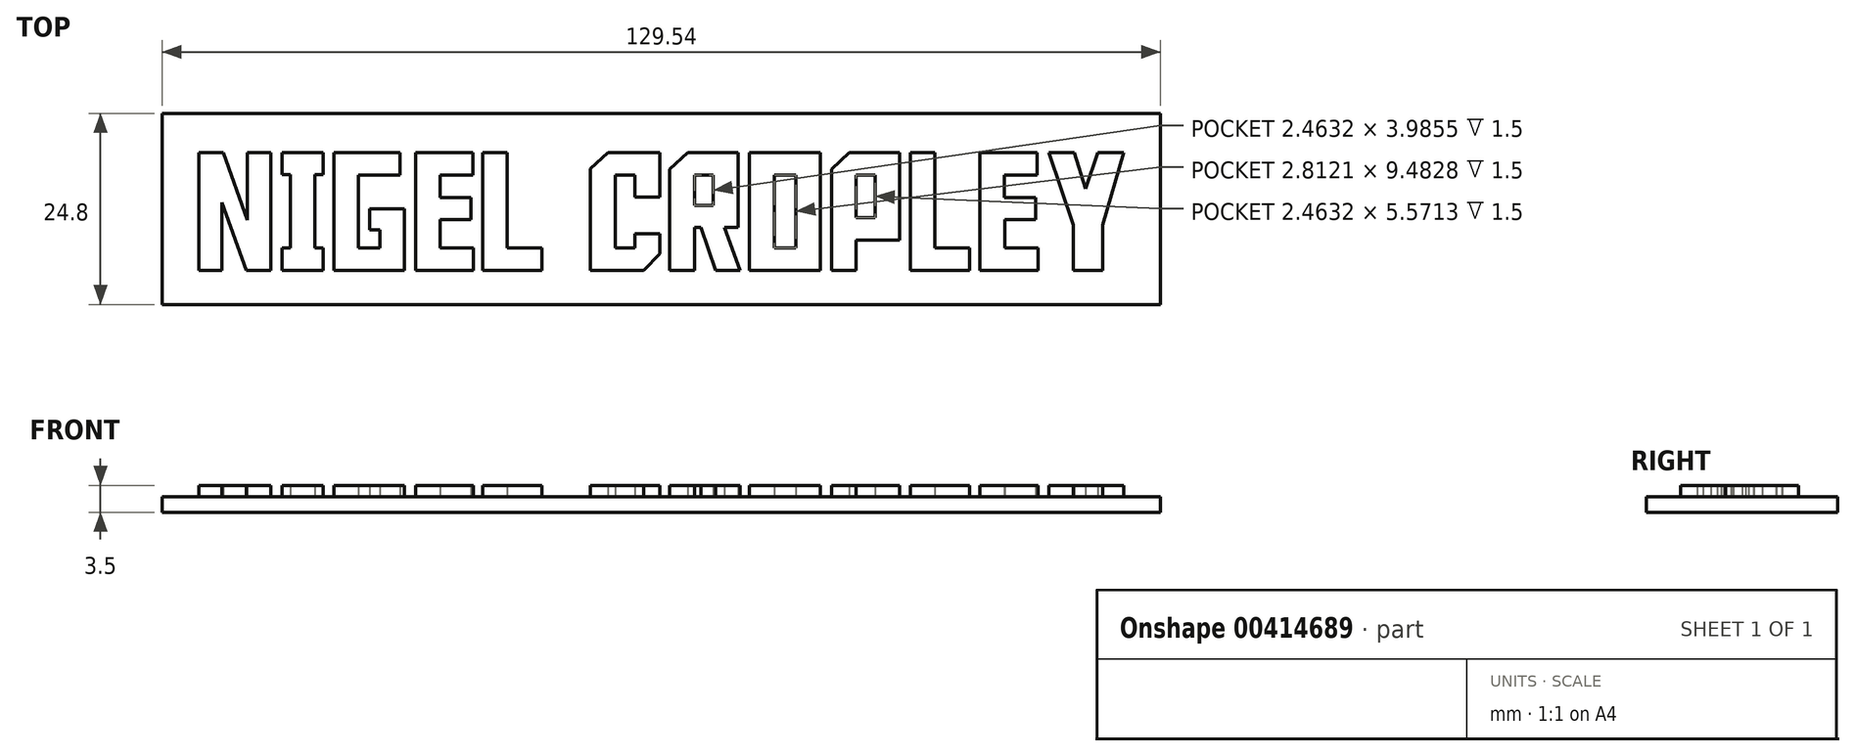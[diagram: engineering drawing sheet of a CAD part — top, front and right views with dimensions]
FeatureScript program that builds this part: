
annotation { "Feature Type Name" : "Feature", "Feature Type Description" : "" }
export const myFeature = defineFeature(function(context is Context, id is Id, definition is map)
    precondition{}
    {
        {
            var Q0;
            Q0=qCreatedBy(makeId("Top.planeOp"),FACE);
            var sketch = newSketch(context, id + "F0", { "sketchPlane" : qUnion([Q0])});
            skLineSegment(sketch, "E0.bottom", {"start": v(-64.77, -12.4) * mm, "end": v(64.77, -12.4) * mm});
            skLineSegment(sketch, "E0.top", {"start": v(-64.77, 12.4) * mm, "end": v(64.77, 12.4) * mm});
            skLineSegment(sketch, "E0.left", {"start": v(-64.77, -12.4) * mm, "end": v(-64.77, 12.4) * mm});
            skLineSegment(sketch, "E0.right", {"start": v(64.77, -12.4) * mm, "end": v(64.77, 12.4) * mm});
            skPoint(sketch, "E0.middle", {"position": v(0, 0) * mm});
            skSolve(sketch);
        }
        {
            var Q0;
            Q0=qCreatedBy(makeId("Top.planeOp"),FACE);
            var sketch = newSketch(context, id + "F1", { "sketchPlane" : qUnion([Q0])});
            skLineSegment(sketch, "E1", {"start": v(-53.72, -1.44) * mm, "end": v(-53.72, 7.33) * mm});
            skLineSegment(sketch, "E2", {"start": v(-53.72, 7.33) * mm, "end": v(-50.7, 7.33) * mm});
            skLineSegment(sketch, "E3", {"start": v(-50.7, 7.33) * mm, "end": v(-50.7, -7.95) * mm});
            skLineSegment(sketch, "E4", {"start": v(-50.7, -7.95) * mm, "end": v(-53.87, -7.95) * mm});
            skLineSegment(sketch, "E5", {"start": v(-53.87, -7.95) * mm, "end": v(-57, 0.82) * mm});
            skLineSegment(sketch, "E6", {"start": v(-57, 0.82) * mm, "end": v(-57, -7.95) * mm});
            skLineSegment(sketch, "E7", {"start": v(-60, -7.95) * mm, "end": v(-60, 7.33) * mm});
            skLineSegment(sketch, "E8", {"start": v(-60, 7.33) * mm, "end": v(-56.83, 7.33) * mm});
            skLineSegment(sketch, "E9", {"start": v(-56.83, 7.33) * mm, "end": v(-53.72, -1.44) * mm});
            skLineSegment(sketch, "E10", {"start": v(-43.88, -5.06) * mm, "end": v(-43.88, -7.95) * mm});
            skLineSegment(sketch, "E11", {"start": v(-43.88, -7.95) * mm, "end": v(-49.2, -7.95) * mm});
            skLineSegment(sketch, "E12", {"start": v(-49.2, -7.95) * mm, "end": v(-49.2, -5.06) * mm});
            skLineSegment(sketch, "E13", {"start": v(-49.2, -5.06) * mm, "end": v(-48.14, -5.06) * mm});
            skLineSegment(sketch, "E14", {"start": v(-48.14, -5.06) * mm, "end": v(-48.14, 4.44) * mm});
            skLineSegment(sketch, "E15", {"start": v(-48.14, 4.44) * mm, "end": v(-49.2, 4.44) * mm});
            skLineSegment(sketch, "E16", {"start": v(-49.2, 4.44) * mm, "end": v(-49.2, 7.33) * mm});
            skLineSegment(sketch, "E17", {"start": v(-49.2, 7.33) * mm, "end": v(-43.88, 7.33) * mm});
            skLineSegment(sketch, "E18", {"start": v(-43.88, 7.33) * mm, "end": v(-43.88, 4.44) * mm});
            skLineSegment(sketch, "E19", {"start": v(-43.88, 4.44) * mm, "end": v(-44.94, 4.44) * mm});
            skLineSegment(sketch, "E20", {"start": v(-44.94, 4.44) * mm, "end": v(-44.94, -5.06) * mm});
            skLineSegment(sketch, "E21", {"start": v(-44.94, -5.06) * mm, "end": v(-43.88, -5.06) * mm});
            skLineSegment(sketch, "E22", {"start": v(-36.54, -5.06) * mm, "end": v(-36.54, -2.7) * mm});
            skLineSegment(sketch, "E23", {"start": v(-36.54, -2.7) * mm, "end": v(-37.84, -2.7) * mm});
            skLineSegment(sketch, "E24", {"start": v(-37.84, -2.7) * mm, "end": v(-37.84, 0.02) * mm});
            skLineSegment(sketch, "E25", {"start": v(-37.84, 0.02) * mm, "end": v(-33.37, 0.02) * mm});
            skLineSegment(sketch, "E26", {"start": v(-33.37, 0.02) * mm, "end": v(-33.37, -7.95) * mm});
            skLineSegment(sketch, "E27", {"start": v(-33.37, -7.95) * mm, "end": v(-42.5, -7.95) * mm});
            skLineSegment(sketch, "E28", {"start": v(-42.5, -7.95) * mm, "end": v(-42.5, 7.33) * mm});
            skLineSegment(sketch, "E29", {"start": v(-42.5, 7.33) * mm, "end": v(-33.9, 7.33) * mm});
            skLineSegment(sketch, "E30", {"start": v(-33.9, 7.33) * mm, "end": v(-33.9, 4.43) * mm});
            skLineSegment(sketch, "E31", {"start": v(-33.9, 4.43) * mm, "end": v(-39.29, 4.43) * mm});
            skLineSegment(sketch, "E32", {"start": v(-39.29, 4.43) * mm, "end": v(-39.29, -5.06) * mm});
            skLineSegment(sketch, "E33", {"start": v(-39.29, -5.06) * mm, "end": v(-36.54, -5.06) * mm});
            skLineSegment(sketch, "E34", {"start": v(-31.9, 7.33) * mm, "end": v(-24.48, 7.33) * mm});
            skLineSegment(sketch, "E35", {"start": v(-24.48, 7.33) * mm, "end": v(-24.48, 4.43) * mm});
            skLineSegment(sketch, "E36", {"start": v(-24.48, 4.43) * mm, "end": v(-28.73, 4.43) * mm});
            skLineSegment(sketch, "E37", {"start": v(-28.73, 4.43) * mm, "end": v(-28.73, 1.48) * mm});
            skLineSegment(sketch, "E38", {"start": v(-28.73, 1.48) * mm, "end": v(-24.7, 1.48) * mm});
            skLineSegment(sketch, "E39", {"start": v(-24.7, 1.48) * mm, "end": v(-24.7, -1.38) * mm});
            skLineSegment(sketch, "E40", {"start": v(-24.7, -1.38) * mm, "end": v(-28.69, -1.38) * mm});
            skLineSegment(sketch, "E41", {"start": v(-28.69, -1.38) * mm, "end": v(-28.69, -5.06) * mm});
            skLineSegment(sketch, "E42", {"start": v(-28.69, -5.06) * mm, "end": v(-24.37, -5.06) * mm});
            skLineSegment(sketch, "E43", {"start": v(-24.37, -5.06) * mm, "end": v(-24.37, -7.95) * mm});
            skLineSegment(sketch, "E44", {"start": v(-24.37, -7.95) * mm, "end": v(-31.9, -7.95) * mm});
            skLineSegment(sketch, "E45", {"start": v(-31.9, -7.95) * mm, "end": v(-31.9, 7.33) * mm});
            skLineSegment(sketch, "E46", {"start": v(-23.2, -7.95) * mm, "end": v(-23.2, 7.33) * mm});
            skLineSegment(sketch, "E47", {"start": v(-23.2, 7.33) * mm, "end": v(-20, 7.33) * mm});
            skLineSegment(sketch, "E48", {"start": v(-20, 7.33) * mm, "end": v(-20, -5.06) * mm});
            skLineSegment(sketch, "E49", {"start": v(-20, -5.06) * mm, "end": v(-15.51, -5.06) * mm});
            skLineSegment(sketch, "E50", {"start": v(-15.51, -5.06) * mm, "end": v(-15.51, -7.95) * mm});
            skLineSegment(sketch, "E51", {"start": v(-15.51, -7.95) * mm, "end": v(-23.2, -7.95) * mm});
            skLineSegment(sketch, "E52", {"start": v(-3.4, -5.06) * mm, "end": v(-3.4, -3.2) * mm});
            skLineSegment(sketch, "E53", {"start": v(-3.4, -3.2) * mm, "end": v(-0.2, -3.2) * mm});
            skLineSegment(sketch, "E54", {"start": v(-0.2, -3.2) * mm, "end": v(-0.2, -5.84) * mm});
            skLineSegment(sketch, "E55", {"start": v(-0.2, -5.84) * mm, "end": v(-2.3, -7.95) * mm});
            skLineSegment(sketch, "E56", {"start": v(-2.3, -7.95) * mm, "end": v(-9.2, -7.95) * mm});
            skLineSegment(sketch, "E57", {"start": v(-9.2, -7.95) * mm, "end": v(-9.2, 5.23) * mm});
            skLineSegment(sketch, "E58", {"start": v(-9.2, 5.23) * mm, "end": v(-6.92, 7.33) * mm});
            skLineSegment(sketch, "E59", {"start": v(-6.92, 7.33) * mm, "end": v(-0.2, 7.33) * mm});
            skLineSegment(sketch, "E60", {"start": v(-0.2, 7.33) * mm, "end": v(-0.2, 1.56) * mm});
            skLineSegment(sketch, "E61", {"start": v(-0.2, 1.56) * mm, "end": v(-3.4, 1.56) * mm});
            skLineSegment(sketch, "E62", {"start": v(-3.4, 1.56) * mm, "end": v(-3.4, 4.43) * mm});
            skLineSegment(sketch, "E63", {"start": v(-3.4, 4.43) * mm, "end": v(-5.99, 4.43) * mm});
            skLineSegment(sketch, "E64", {"start": v(-5.99, 4.43) * mm, "end": v(-5.99, -5.06) * mm});
            skLineSegment(sketch, "E65", {"start": v(-5.99, -5.06) * mm, "end": v(-3.4, -5.06) * mm});
            skLineSegment(sketch, "E66", {"start": v(7.04, -7.95) * mm, "end": v(5.13, -2.42) * mm});
            skLineSegment(sketch, "E67", {"start": v(5.13, -2.42) * mm, "end": v(4.29, -2.42) * mm});
            skLineSegment(sketch, "E68", {"start": v(4.29, -2.42) * mm, "end": v(4.29, -7.95) * mm});
            skLineSegment(sketch, "E69", {"start": v(4.29, -7.95) * mm, "end": v(1.08, -7.95) * mm});
            skLineSegment(sketch, "E70", {"start": v(1.08, -7.95) * mm, "end": v(1.08, 5.18) * mm});
            skLineSegment(sketch, "E71", {"start": v(1.08, 5.18) * mm, "end": v(3.4, 7.33) * mm});
            skLineSegment(sketch, "E72", {"start": v(3.4, 7.33) * mm, "end": v(9.95, 7.33) * mm});
            skLineSegment(sketch, "E73", {"start": v(9.95, 7.33) * mm, "end": v(9.95, -2.38) * mm});
            skLineSegment(sketch, "E74", {"start": v(9.95, -2.38) * mm, "end": v(8.22, -2.38) * mm});
            skLineSegment(sketch, "E75", {"start": v(8.22, -2.38) * mm, "end": v(10.25, -7.95) * mm});
            skLineSegment(sketch, "E76", {"start": v(10.25, -7.95) * mm, "end": v(7.04, -7.95) * mm});
            skLineSegment(sketch, "E77", {"start": v(6.75, 0.44) * mm, "end": v(6.75, 4.43) * mm});
            skLineSegment(sketch, "E78", {"start": v(6.75, 4.43) * mm, "end": v(4.29, 4.43) * mm});
            skLineSegment(sketch, "E79", {"start": v(4.29, 4.43) * mm, "end": v(4.29, 0.44) * mm});
            skLineSegment(sketch, "E80", {"start": v(4.29, 0.44) * mm, "end": v(6.75, 0.44) * mm});
            skLineSegment(sketch, "E81", {"start": v(11.43, 7.33) * mm, "end": v(20.66, 7.33) * mm});
            skLineSegment(sketch, "E82", {"start": v(20.66, 7.33) * mm, "end": v(20.66, -7.95) * mm});
            skLineSegment(sketch, "E83", {"start": v(20.66, -7.95) * mm, "end": v(11.43, -7.95) * mm});
            skLineSegment(sketch, "E84", {"start": v(11.43, -7.95) * mm, "end": v(11.43, 7.33) * mm});
            skLineSegment(sketch, "E85", {"start": v(14.65, -5.06) * mm, "end": v(17.46, -5.06) * mm});
            skLineSegment(sketch, "E86", {"start": v(17.46, -5.06) * mm, "end": v(17.46, 4.43) * mm});
            skLineSegment(sketch, "E87", {"start": v(17.46, 4.43) * mm, "end": v(14.65, 4.43) * mm});
            skLineSegment(sketch, "E88", {"start": v(14.65, 4.43) * mm, "end": v(14.65, -5.06) * mm});
            skLineSegment(sketch, "E89", {"start": v(25.27, -7.95) * mm, "end": v(22.07, -7.95) * mm});
            skLineSegment(sketch, "E90", {"start": v(22.07, -7.95) * mm, "end": v(22.07, 5.18) * mm});
            skLineSegment(sketch, "E91", {"start": v(22.07, 5.18) * mm, "end": v(24.38, 7.33) * mm});
            skLineSegment(sketch, "E92", {"start": v(24.38, 7.33) * mm, "end": v(30.94, 7.33) * mm});
            skLineSegment(sketch, "E93", {"start": v(30.94, 7.33) * mm, "end": v(30.94, -4.07) * mm});
            skLineSegment(sketch, "E94", {"start": v(30.94, -4.07) * mm, "end": v(25.27, -4.07) * mm});
            skLineSegment(sketch, "E95", {"start": v(25.27, -4.07) * mm, "end": v(25.27, -7.95) * mm});
            skLineSegment(sketch, "E96", {"start": v(27.74, -1.14) * mm, "end": v(27.74, 4.43) * mm});
            skLineSegment(sketch, "E97", {"start": v(27.74, 4.43) * mm, "end": v(25.27, 4.43) * mm});
            skLineSegment(sketch, "E98", {"start": v(25.27, 4.43) * mm, "end": v(25.27, -1.14) * mm});
            skLineSegment(sketch, "E99", {"start": v(25.27, -1.14) * mm, "end": v(27.74, -1.14) * mm});
            skLineSegment(sketch, "E100", {"start": v(32.3, -7.95) * mm, "end": v(32.3, 7.33) * mm});
            skLineSegment(sketch, "E101", {"start": v(32.3, 7.33) * mm, "end": v(35.5, 7.33) * mm});
            skLineSegment(sketch, "E102", {"start": v(35.5, 7.33) * mm, "end": v(35.5, -5.06) * mm});
            skLineSegment(sketch, "E103", {"start": v(35.5, -5.06) * mm, "end": v(39.99, -5.06) * mm});
            skLineSegment(sketch, "E104", {"start": v(39.99, -5.06) * mm, "end": v(39.99, -7.95) * mm});
            skLineSegment(sketch, "E105", {"start": v(39.99, -7.95) * mm, "end": v(32.3, -7.95) * mm});
            skLineSegment(sketch, "E106", {"start": v(41.36, 7.33) * mm, "end": v(48.78, 7.33) * mm});
            skLineSegment(sketch, "E107", {"start": v(48.78, 7.33) * mm, "end": v(48.78, 4.43) * mm});
            skLineSegment(sketch, "E108", {"start": v(48.78, 4.43) * mm, "end": v(44.53, 4.43) * mm});
            skLineSegment(sketch, "E109", {"start": v(44.53, 4.43) * mm, "end": v(44.53, 1.48) * mm});
            skLineSegment(sketch, "E110", {"start": v(44.53, 1.48) * mm, "end": v(48.57, 1.48) * mm});
            skLineSegment(sketch, "E111", {"start": v(48.57, 1.48) * mm, "end": v(48.57, -1.38) * mm});
            skLineSegment(sketch, "E112", {"start": v(48.57, -1.38) * mm, "end": v(44.58, -1.38) * mm});
            skLineSegment(sketch, "E113", {"start": v(44.58, -1.38) * mm, "end": v(44.58, -5.06) * mm});
            skLineSegment(sketch, "E114", {"start": v(44.58, -5.06) * mm, "end": v(48.89, -5.06) * mm});
            skLineSegment(sketch, "E115", {"start": v(48.89, -5.06) * mm, "end": v(48.89, -7.95) * mm});
            skLineSegment(sketch, "E116", {"start": v(48.89, -7.95) * mm, "end": v(41.36, -7.95) * mm});
            skLineSegment(sketch, "E117", {"start": v(41.36, -7.95) * mm, "end": v(41.36, 7.33) * mm});
            skLineSegment(sketch, "E118", {"start": v(56.67, 7.33) * mm, "end": v(60, 7.33) * mm});
            skLineSegment(sketch, "E119", {"start": v(53.48, -2.1) * mm, "end": v(50.27, 7.33) * mm});
            skLineSegment(sketch, "E120", {"start": v(50.27, 7.33) * mm, "end": v(53.58, 7.33) * mm});
            skLineSegment(sketch, "E121", {"start": v(53.58, 7.33) * mm, "end": v(55.06, 2.6) * mm});
            skLineSegment(sketch, "E122", {"start": v(55.06, 2.6) * mm, "end": v(56.67, 7.33) * mm});
            skLineSegment(sketch, "E123", {"start": v(-60, -7.95) * mm, "end": v(-57, -7.95) * mm});
            skLineSegment(sketch, "E124", {"start": v(53.48, -2.1) * mm, "end": v(53.48, -7.95) * mm});
            skLineSegment(sketch, "E125", {"start": v(53.48, -7.95) * mm, "end": v(57.28, -7.95) * mm});
            skLineSegment(sketch, "E126", {"start": v(57.28, -7.95) * mm, "end": v(57.28, -2.1) * mm});
            skLineSegment(sketch, "E127", {"start": v(57.28, -2.1) * mm, "end": v(60, 7.33) * mm});
            skSolve(sketch);
        }
        {
            var Q0;
            Q0 = qSketchRegion(id + "F0", true);
            extrude(context, id + "F2", {"entities" : qUnion([Q0]), "oppositeDirection" : true, "depth" : 2 * mm});
        }
        {
            var Q0;
            Q0 = qSketchRegion(id + "F1", true);
            extrude(context, id + "F3", {"entities" : qUnion([Q0]), "operationType" : NewBodyOperationType.ADD, "depth" : 1.5 * mm});
        }
    });
